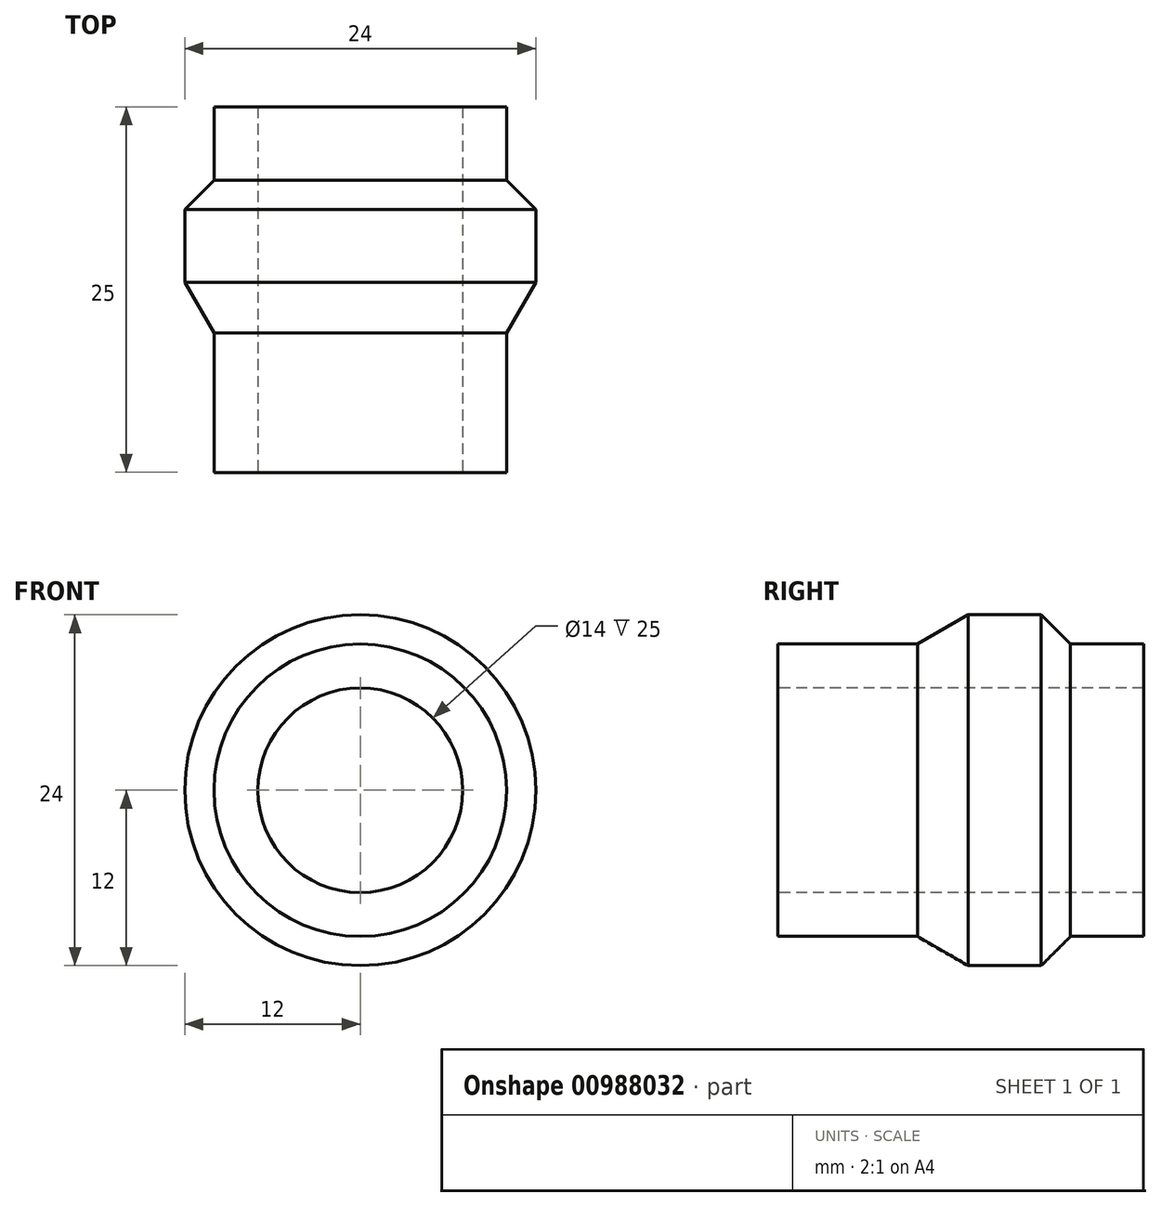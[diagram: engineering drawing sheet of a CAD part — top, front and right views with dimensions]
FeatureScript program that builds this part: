
annotation { "Feature Type Name" : "Feature", "Feature Type Description" : "" }
export const myFeature = defineFeature(function(context is Context, id is Id, definition is map)
    precondition{}
    {
        {
            var Q0;
            Q0=qCreatedBy(makeId("Right.planeOp"),FACE);
            var sketch = newSketch(context, id + "F0", { "sketchPlane" : qUnion([Q0])});
            skLineSegment(sketch, "E0", {"start": v(12.39, 10) * mm, "end": v(7.39, 10) * mm});
            skLineSegment(sketch, "E1", {"start": v(7.39, 10) * mm, "end": v(5.39, 12) * mm});
            skLineSegment(sketch, "E2", {"start": v(5.39, 12) * mm, "end": v(0.39, 12) * mm});
            skLineSegment(sketch, "E3", {"start": v(0.39, 12) * mm, "end": v(-3.08, 10) * mm});
            skLineSegment(sketch, "E4", {"start": v(-3.08, 10) * mm, "end": v(-12.61, 10) * mm});
            skLineSegment(sketch, "E5", {"start": v(12.39, 7) * mm, "end": v(12.39, 10) * mm});
            skLineSegment(sketch, "E6", {"start": v(-12.61, 10) * mm, "end": v(-12.61, 7) * mm});
            skLineSegment(sketch, "E7", {"start": v(-12.61, 7) * mm, "end": v(12.39, 7) * mm});
            skSolve(sketch);
        }
        {
            var Q0;
            Q0=qCreatedBy(makeId("Right.planeOp"),FACE);
            var sketch = newSketch(context, id + "F1", { "sketchPlane" : qUnion([Q0])});
            skLineSegment(sketch, "E8", {"start": v(-67.48, 0) * mm, "end": v(42.56, 0) * mm, "construction": true});
            skSolve(sketch);
        }
        {
            var Q0;
            Q0=makeQuery(id+"F0.imprint","IMPRINT",FACE,{"disambiguationData":[TD([[makeQuery(id+"F0.imprint","IMPRINT",EDGE,{"derivedFrom":sQuery(id+"F0.wireOp",EDGE,"E0")}),1.0]])]});
            var Q1;
            Q1=sQuery(id+"F1.wireOp",EDGE,"E8");
            revolve(context, id + "F2", {"surfaceOperationType" : NewSurfaceOperationType.NEW, "entities" : qUnion([Q0]), "axis" : qUnion([Q1]), "revolveType" : RevolveType.FULL});
        }
    });
